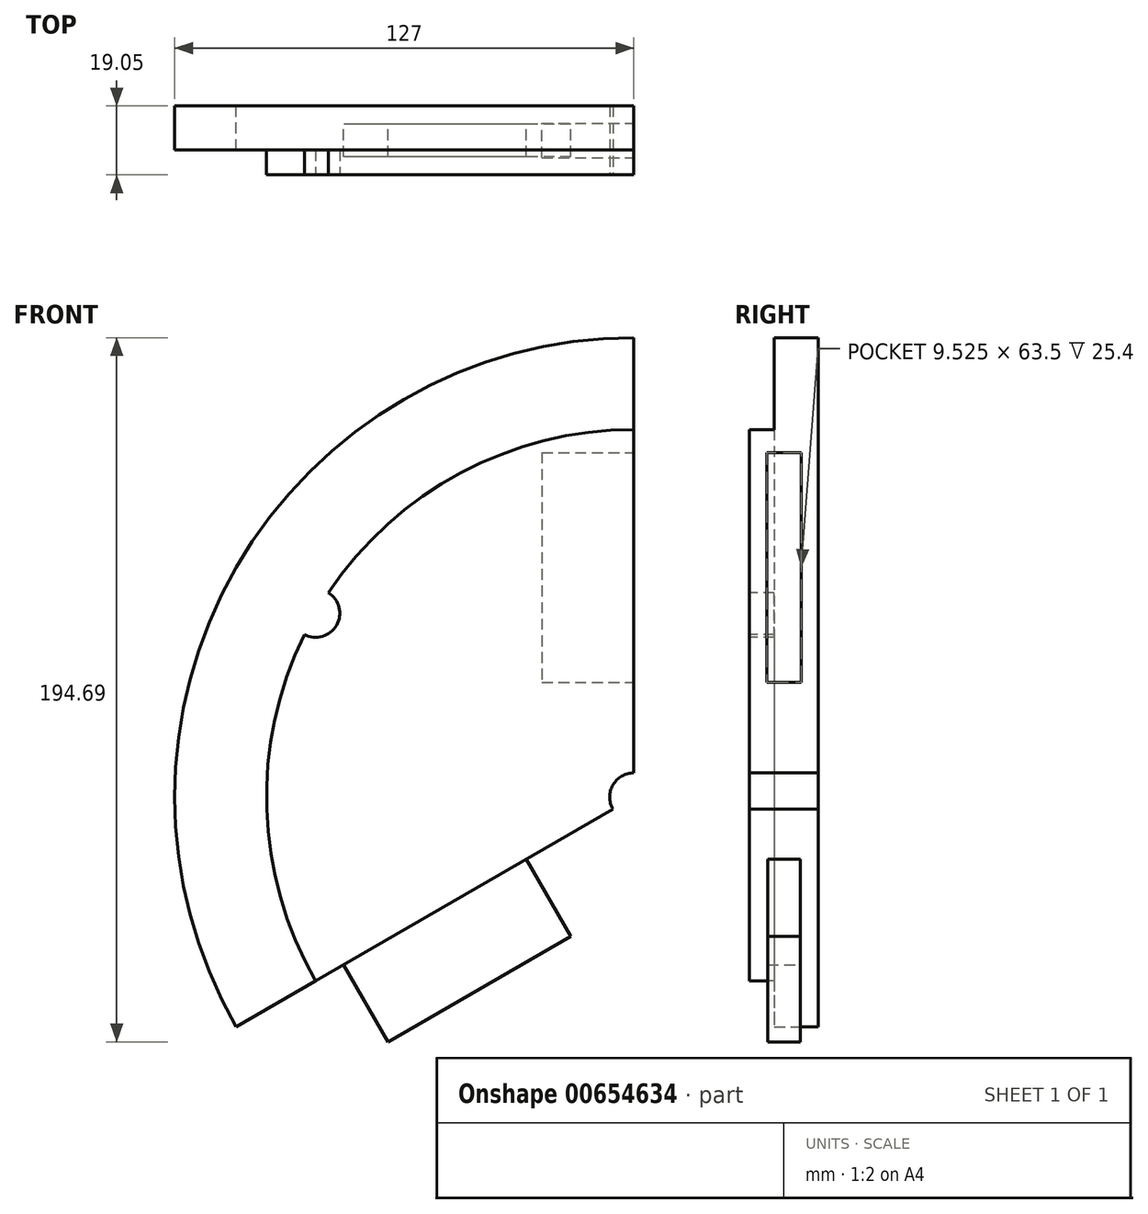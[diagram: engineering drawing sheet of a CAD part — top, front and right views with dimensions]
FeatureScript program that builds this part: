
annotation { "Feature Type Name" : "Feature", "Feature Type Description" : "" }
export const myFeature = defineFeature(function(context is Context, id is Id, definition is map)
    precondition{}
    {
        {
            var Q0;
            Q0=qCreatedBy(makeId("Front.planeOp"),FACE);
            var sketch = newSketch(context, id + "F0", { "sketchPlane" : qUnion([Q0])});
            skArc(sketch, "E0", {"start": v(0, 127) * mm, "mid": v(-109.99, 63.5) * mm, "end": v(-109.99, -63.5) * mm});
            skLineSegment(sketch, "E1", {"start": v(0, 0) * mm, "end": v(0, 127) * mm});
            skLineSegment(sketch, "E2", {"start": v(0, 0) * mm, "end": v(-109.99, -63.5) * mm});
            skArc(sketch, "E3", {"start": v(0, 101.6) * mm, "mid": v(-87.99, 50.8) * mm, "end": v(-87.99, -50.8) * mm});
            skLineSegment(sketch, "E4", {"start": v(0, 0) * mm, "end": v(-109.99, 63.5) * mm});
            skLineSegment(sketch, "E5", {"start": v(0, 0) * mm, "end": v(-63.5, 109.99) * mm});
            skLineSegment(sketch, "E6", {"start": v(0, 0) * mm, "end": v(-127, 0) * mm});
            skCircle(sketch, "E7", {"center": v(-50.8, 87.99) * mm, "radius": 6.6 * mm});
            skCircle(sketch, "E8", {"center": v(-101.6, 0) * mm, "radius": 6.6 * mm});
            skCircle(sketch, "E9", {"center": v(-87.99, 50.8) * mm, "radius": 6.6 * mm});
            skSolve(sketch);
        }
        {
            var Q0;
            {var subQ1=sQuery(id+"F0.wireOp",EDGE,"E0");var subQ6=sQuery(id+"F0.wireOp",EDGE,"E1");var subQ9=makeQuery(id+"F0.imprint","INTERSECT",VERTEX,{"derivedFrom":[subQ1,subQ6]});Q0=makeQuery(id+"F0.imprint","IMPRINT",FACE,{"disambiguationData":[TD([[makeQuery(id+"F0.imprint","IMPRINT",EDGE,{"disambiguationData":[TD([[subQ9,-1.0]])],"derivedFrom":subQ1}),1.0]])]});}
            var Q1;
            {var subQ1=sQuery(id+"F0.wireOp",EDGE,"E0");var subQ6=sQuery(id+"F0.wireOp",EDGE,"E2");var subQ9=makeQuery(id+"F0.imprint","INTERSECT",VERTEX,{"derivedFrom":[subQ1,subQ6]});Q1=makeQuery(id+"F0.imprint","IMPRINT",FACE,{"disambiguationData":[TD([[makeQuery(id+"F0.imprint","IMPRINT",EDGE,{"disambiguationData":[TD([[subQ9,1.0]])],"derivedFrom":subQ1}),1.0]])]});}
            var Q2;
            {var subQ1=sQuery(id+"F0.wireOp",EDGE,"E1");var subQ3=sQuery(id+"F0.wireOp",EDGE,"E3");var subQ4=makeQuery(id+"F0.imprint","INTERSECT",VERTEX,{"derivedFrom":[subQ1,subQ3]});Q2=makeQuery(id+"F0.imprint","IMPRINT",FACE,{"disambiguationData":[TD([[makeQuery(id+"F0.imprint","IMPRINT",EDGE,{"disambiguationData":[TD([[subQ4,-1.0]])],"derivedFrom":subQ3}),1.0]])]});}
            var Q3;
            {var subQ1=sQuery(id+"F0.wireOp",EDGE,"E2");var subQ3=sQuery(id+"F0.wireOp",EDGE,"E3");var subQ4=makeQuery(id+"F0.imprint","INTERSECT",VERTEX,{"derivedFrom":[subQ1,subQ3]});Q3=makeQuery(id+"F0.imprint","IMPRINT",FACE,{"disambiguationData":[TD([[makeQuery(id+"F0.imprint","IMPRINT",EDGE,{"disambiguationData":[TD([[subQ4,1.0]])],"derivedFrom":subQ3}),1.0]])]});}
            var Q4;
            {var subQ0=sQuery(id+"F0.wireOp",EDGE,"E4");var subQ1=sQuery(id+"F0.wireOp",EDGE,"E0");var subQ2=makeQuery(id+"F0.imprint","INTERSECT",VERTEX,{"derivedFrom":[subQ1,subQ0]});Q4=makeQuery(id+"F0.imprint","IMPRINT",FACE,{"disambiguationData":[TD([[makeQuery(id+"F0.imprint","IMPRINT",EDGE,{"disambiguationData":[TD([[subQ2,1.0]])],"derivedFrom":subQ1}),1.0]])]});}
            var Q5;
            {var subQ1=sQuery(id+"F0.wireOp",EDGE,"E0");var subQ9=sQuery(id+"F0.wireOp",EDGE,"E4");var subQ10=makeQuery(id+"F0.imprint","INTERSECT",VERTEX,{"derivedFrom":[subQ1,subQ9]});Q5=makeQuery(id+"F0.imprint","IMPRINT",FACE,{"disambiguationData":[TD([[makeQuery(id+"F0.imprint","IMPRINT",EDGE,{"disambiguationData":[TD([[subQ10,-1.0]])],"derivedFrom":subQ1}),1.0]])]});}
            var Q6;
            {var subQ0=sQuery(id+"F0.wireOp",EDGE,"E7");var subQ1=sQuery(id+"F0.wireOp",EDGE,"E3");var subQ2=makeQuery(id+"F0.imprint","INTERSECT",VERTEX,{"disambiguationData":[OD(1.0)],"derivedFrom":[subQ1,subQ0]});Q6=makeQuery(id+"F0.imprint","IMPRINT",FACE,{"disambiguationData":[TD([[makeQuery(id+"F0.imprint","IMPRINT",EDGE,{"disambiguationData":[TD([[subQ2,-1.0]])],"derivedFrom":subQ1}),1.0]])]});}
            var Q7;
            {var subQ1=sQuery(id+"F0.wireOp",EDGE,"E3");var subQ7=sQuery(id+"F0.wireOp",EDGE,"E9");var subQ9=makeQuery(id+"F0.imprint","INTERSECT",VERTEX,{"disambiguationData":[OD(1.0)],"derivedFrom":[subQ1,subQ7]});Q7=makeQuery(id+"F0.imprint","IMPRINT",FACE,{"disambiguationData":[TD([[makeQuery(id+"F0.imprint","IMPRINT",EDGE,{"disambiguationData":[TD([[subQ9,-1.0]])],"derivedFrom":subQ1}),1.0]])]});}
            var Q8;
            {var subQ0=sQuery(id+"F0.wireOp",EDGE,"E6");var subQ1=sQuery(id+"F0.wireOp",EDGE,"E3");var subQ2=makeQuery(id+"F0.imprint","INTERSECT",VERTEX,{"derivedFrom":[subQ1,subQ0]});Q8=makeQuery(id+"F0.imprint","IMPRINT",FACE,{"disambiguationData":[TD([[makeQuery(id+"F0.imprint","IMPRINT",EDGE,{"disambiguationData":[TD([[subQ2,-1.0]])],"derivedFrom":subQ1}),-1.0]])]});}
            var Q9;
            {var subQ0=sQuery(id+"F0.wireOp",EDGE,"E6");var subQ1=sQuery(id+"F0.wireOp",EDGE,"E3");var subQ2=makeQuery(id+"F0.imprint","INTERSECT",VERTEX,{"derivedFrom":[subQ1,subQ0]});Q9=makeQuery(id+"F0.imprint","IMPRINT",FACE,{"disambiguationData":[TD([[makeQuery(id+"F0.imprint","IMPRINT",EDGE,{"disambiguationData":[TD([[subQ2,-1.0]])],"derivedFrom":subQ1}),1.0]])]});}
            var Q10;
            {var subQ0=sQuery(id+"F0.wireOp",EDGE,"E8");var subQ1=sQuery(id+"F0.wireOp",EDGE,"E3");var subQ2=makeQuery(id+"F0.imprint","INTERSECT",VERTEX,{"disambiguationData":[OD(0.0)],"derivedFrom":[subQ1,subQ0]});Q10=makeQuery(id+"F0.imprint","IMPRINT",FACE,{"disambiguationData":[TD([[makeQuery(id+"F0.imprint","IMPRINT",EDGE,{"disambiguationData":[TD([[subQ2,-1.0]])],"derivedFrom":subQ1}),-1.0]])]});}
            var Q11;
            {var subQ0=sQuery(id+"F0.wireOp",EDGE,"E8");var subQ1=sQuery(id+"F0.wireOp",EDGE,"E3");var subQ2=makeQuery(id+"F0.imprint","INTERSECT",VERTEX,{"disambiguationData":[OD(0.0)],"derivedFrom":[subQ1,subQ0]});Q11=makeQuery(id+"F0.imprint","IMPRINT",FACE,{"disambiguationData":[TD([[makeQuery(id+"F0.imprint","IMPRINT",EDGE,{"disambiguationData":[TD([[subQ2,-1.0]])],"derivedFrom":subQ1}),1.0]])]});}
            var Q12;
            {var subQ0=sQuery(id+"F0.wireOp",EDGE,"E4");var subQ1=sQuery(id+"F0.wireOp",EDGE,"E3");var subQ2=makeQuery(id+"F0.imprint","INTERSECT",VERTEX,{"derivedFrom":[subQ1,subQ0]});Q12=makeQuery(id+"F0.imprint","IMPRINT",FACE,{"disambiguationData":[TD([[makeQuery(id+"F0.imprint","IMPRINT",EDGE,{"disambiguationData":[TD([[subQ2,-1.0]])],"derivedFrom":subQ1}),1.0]])]});}
            var Q13;
            {var subQ0=sQuery(id+"F0.wireOp",EDGE,"E4");var subQ1=sQuery(id+"F0.wireOp",EDGE,"E3");var subQ2=makeQuery(id+"F0.imprint","INTERSECT",VERTEX,{"derivedFrom":[subQ1,subQ0]});Q13=makeQuery(id+"F0.imprint","IMPRINT",FACE,{"disambiguationData":[TD([[makeQuery(id+"F0.imprint","IMPRINT",EDGE,{"disambiguationData":[TD([[subQ2,-1.0]])],"derivedFrom":subQ1}),-1.0]])]});}
            var Q14;
            {var subQ0=sQuery(id+"F0.wireOp",EDGE,"E9");var subQ1=sQuery(id+"F0.wireOp",EDGE,"E3");var subQ2=makeQuery(id+"F0.imprint","INTERSECT",VERTEX,{"disambiguationData":[OD(0.0)],"derivedFrom":[subQ1,subQ0]});Q14=makeQuery(id+"F0.imprint","IMPRINT",FACE,{"disambiguationData":[TD([[makeQuery(id+"F0.imprint","IMPRINT",EDGE,{"disambiguationData":[TD([[subQ2,-1.0]])],"derivedFrom":subQ1}),-1.0]])]});}
            var Q15;
            {var subQ0=sQuery(id+"F0.wireOp",EDGE,"E9");var subQ1=sQuery(id+"F0.wireOp",EDGE,"E3");var subQ2=makeQuery(id+"F0.imprint","INTERSECT",VERTEX,{"disambiguationData":[OD(0.0)],"derivedFrom":[subQ1,subQ0]});Q15=makeQuery(id+"F0.imprint","IMPRINT",FACE,{"disambiguationData":[TD([[makeQuery(id+"F0.imprint","IMPRINT",EDGE,{"disambiguationData":[TD([[subQ2,-1.0]])],"derivedFrom":subQ1}),1.0]])]});}
            var Q16;
            {var subQ0=sQuery(id+"F0.wireOp",EDGE,"E5");var subQ1=sQuery(id+"F0.wireOp",EDGE,"E3");var subQ2=makeQuery(id+"F0.imprint","INTERSECT",VERTEX,{"derivedFrom":[subQ1,subQ0]});Q16=makeQuery(id+"F0.imprint","IMPRINT",FACE,{"disambiguationData":[TD([[makeQuery(id+"F0.imprint","IMPRINT",EDGE,{"disambiguationData":[TD([[subQ2,-1.0]])],"derivedFrom":subQ1}),1.0]])]});}
            var Q17;
            {var subQ0=sQuery(id+"F0.wireOp",EDGE,"E7");var subQ1=sQuery(id+"F0.wireOp",EDGE,"E3");var subQ2=makeQuery(id+"F0.imprint","INTERSECT",VERTEX,{"disambiguationData":[OD(0.0)],"derivedFrom":[subQ1,subQ0]});Q17=makeQuery(id+"F0.imprint","IMPRINT",FACE,{"disambiguationData":[TD([[makeQuery(id+"F0.imprint","IMPRINT",EDGE,{"disambiguationData":[TD([[subQ2,-1.0]])],"derivedFrom":subQ1}),1.0]])]});}
            var Q18;
            {var subQ0=sQuery(id+"F0.wireOp",EDGE,"E7");var subQ1=sQuery(id+"F0.wireOp",EDGE,"E3");var subQ2=makeQuery(id+"F0.imprint","INTERSECT",VERTEX,{"disambiguationData":[OD(0.0)],"derivedFrom":[subQ1,subQ0]});Q18=makeQuery(id+"F0.imprint","IMPRINT",FACE,{"disambiguationData":[TD([[makeQuery(id+"F0.imprint","IMPRINT",EDGE,{"disambiguationData":[TD([[subQ2,-1.0]])],"derivedFrom":subQ1}),-1.0]])]});}
            var Q19;
            {var subQ0=sQuery(id+"F0.wireOp",EDGE,"E5");var subQ1=sQuery(id+"F0.wireOp",EDGE,"E3");var subQ2=makeQuery(id+"F0.imprint","INTERSECT",VERTEX,{"derivedFrom":[subQ1,subQ0]});Q19=makeQuery(id+"F0.imprint","IMPRINT",FACE,{"disambiguationData":[TD([[makeQuery(id+"F0.imprint","IMPRINT",EDGE,{"disambiguationData":[TD([[subQ2,-1.0]])],"derivedFrom":subQ1}),-1.0]])]});}
            extrude(context, id + "F1", {"entities" : qUnion([Q0, Q1, Q2, Q3, Q4, Q5, Q6, Q7, Q8, Q9, Q10, Q11, Q12, Q13, Q14, Q15, Q16, Q17, Q18, Q19]), "depth" : 19.05 * mm, "offsetDistance" : 25.4 * mm});
        }
        {
            var Q0;
            Q0=makeQuery(id+"F1.opExtrude","SWEPT_FACE",FACE,{"disambiguationData":[OSD([sQuery(id+"F0.wireOp",EDGE,"E1")])]});
            var sketch = newSketch(context, id + "F2", { "sketchPlane" : qUnion([Q0])});
            skLineSegment(sketch, "E10.bottom", {"start": v(0, 0) * mm, "end": v(-19.05, 0) * mm});
            skLineSegment(sketch, "E10.top", {"start": v(0, 127) * mm, "end": v(-19.05, 127) * mm});
            skLineSegment(sketch, "E10.left", {"start": v(0, 0) * mm, "end": v(0, 127) * mm});
            skLineSegment(sketch, "E10.right", {"start": v(-19.05, 0) * mm, "end": v(-19.05, 127) * mm});
            skLineSegment(sketch, "E11", {"start": v(-9.53, 0) * mm, "end": v(-9.53, 127) * mm});
            skLineSegment(sketch, "E12", {"start": v(-19.05, 63.5) * mm, "end": v(0, 63.5) * mm});
            skPoint(sketch, "E13", {"position": v(-9.53, 63.5) * mm});
            skLineSegment(sketch, "E14.bottom", {"start": v(-14.29, 95.25) * mm, "end": v(-4.76, 95.25) * mm});
            skLineSegment(sketch, "E14.top", {"start": v(-14.29, 31.75) * mm, "end": v(-4.76, 31.75) * mm});
            skLineSegment(sketch, "E14.left", {"start": v(-14.29, 95.25) * mm, "end": v(-14.29, 31.75) * mm});
            skLineSegment(sketch, "E14.right", {"start": v(-4.76, 95.25) * mm, "end": v(-4.76, 31.75) * mm});
            skSolve(sketch);
        }
        {
            var Q0;
            {var subQ0=sQuery(id+"F2.wireOp",EDGE,"E14.top");var subQ1=sQuery(id+"F2.wireOp",EDGE,"E11");var subQ2=makeQuery(id+"F2.imprint","INTERSECT",VERTEX,{"derivedFrom":[subQ1,subQ0]});Q0=makeQuery(id+"F2.imprint","IMPRINT",FACE,{"disambiguationData":[TD([[makeQuery(id+"F2.imprint","IMPRINT",EDGE,{"disambiguationData":[TD([[subQ2,-1.0]])],"derivedFrom":subQ1}),-1.0]])]});}
            var Q1;
            {var subQ0=sQuery(id+"F2.wireOp",EDGE,"E14.top");var subQ1=sQuery(id+"F2.wireOp",EDGE,"E11");var subQ2=makeQuery(id+"F2.imprint","INTERSECT",VERTEX,{"derivedFrom":[subQ1,subQ0]});Q1=makeQuery(id+"F2.imprint","IMPRINT",FACE,{"disambiguationData":[TD([[makeQuery(id+"F2.imprint","IMPRINT",EDGE,{"disambiguationData":[TD([[subQ2,-1.0]])],"derivedFrom":subQ1}),1.0]])]});}
            var Q2;
            {var subQ0=sQuery(id+"F2.wireOp",EDGE,"E12");var subQ1=sQuery(id+"F2.wireOp",EDGE,"E11");var subQ2=makeQuery(id+"F2.imprint","INTERSECT",VERTEX,{"derivedFrom":[subQ1,subQ0]});Q2=makeQuery(id+"F2.imprint","IMPRINT",FACE,{"disambiguationData":[TD([[makeQuery(id+"F2.imprint","IMPRINT",EDGE,{"disambiguationData":[TD([[subQ2,-1.0]])],"derivedFrom":subQ1}),1.0]])]});}
            var Q3;
            {var subQ0=sQuery(id+"F2.wireOp",EDGE,"E12");var subQ1=sQuery(id+"F2.wireOp",EDGE,"E11");var subQ2=makeQuery(id+"F2.imprint","INTERSECT",VERTEX,{"derivedFrom":[subQ1,subQ0]});Q3=makeQuery(id+"F2.imprint","IMPRINT",FACE,{"disambiguationData":[TD([[makeQuery(id+"F2.imprint","IMPRINT",EDGE,{"disambiguationData":[TD([[subQ2,-1.0]])],"derivedFrom":subQ1}),-1.0]])]});}
            extrude(context, id + "F3", {"entities" : qUnion([Q0, Q1, Q2, Q3]), "operationType" : NewBodyOperationType.REMOVE, "oppositeDirection" : true, "depth" : 25.4 * mm, "offsetDistance" : 25.4 * mm});
        }
        {
            var Q0;
            Q0=makeQuery(id+"F1.opExtrude","SWEPT_FACE",FACE,{"disambiguationData":[OSD([sQuery(id+"F0.wireOp",EDGE,"E2")])]});
            var sketch = newSketch(context, id + "F4", { "sketchPlane" : qUnion([Q0])});
            skLineSegment(sketch, "E15", {"start": v(-63.5, 0) * mm, "end": v(-63.5, 19.05) * mm});
            skLineSegment(sketch, "E16.bottom", {"start": v(-34.29, 14.03) * mm, "end": v(-92.7, 14.03) * mm});
            skLineSegment(sketch, "E16.top", {"start": v(-34.29, 5.02) * mm, "end": v(-92.7, 5.02) * mm});
            skLineSegment(sketch, "E16.left", {"start": v(-34.29, 14.03) * mm, "end": v(-34.29, 5.02) * mm});
            skLineSegment(sketch, "E16.right", {"start": v(-92.7, 14.03) * mm, "end": v(-92.7, 5.02) * mm});
            skPoint(sketch, "E16.middle", {"position": v(-63.5, 9.53) * mm});
            skSolve(sketch);
        }
        {
            var Q0;
            Q0 = qSketchRegion(id + "F4", true);
            extrude(context, id + "F5", {"entities" : qUnion([Q0]), "operationType" : NewBodyOperationType.ADD, "depth" : 24.64 * mm, "offsetDistance" : 25.4 * mm});
        }
        {
            var Q0;
            Q0=makeQuery(id+"F1.opExtrude","CAP_FACE",FACE,{"disambiguationData":[OSD([sQuery(id+"F0.wireOp",EDGE,"E0"),sQuery(id+"F0.wireOp",EDGE,"E1"),sQuery(id+"F0.wireOp",EDGE,"E2")])],"isStart":false});
            var sketch = newSketch(context, id + "F6", { "sketchPlane" : qUnion([Q0])});
            skLineSegment(sketch, "E17", {"start": v(0, 0) * mm, "end": v(-109.99, 63.5) * mm});
            skLineSegment(sketch, "E18", {"start": v(0, 0) * mm, "end": v(-63.5, 109.99) * mm});
            skLineSegment(sketch, "E19", {"start": v(0, 0) * mm, "end": v(-127, 0) * mm});
            skCircle(sketch, "E20", {"center": v(0, 0) * mm, "radius": 10.16 * mm});
            skCircle(sketch, "E21", {"center": v(0, 0) * mm, "radius": 101.6 * mm});
            skCircle(sketch, "E22", {"center": v(-50.8, 87.99) * mm, "radius": 6.66 * mm});
            skCircle(sketch, "E23", {"center": v(-87.99, 50.8) * mm, "radius": 6.67 * mm});
            skCircle(sketch, "E24", {"center": v(-101.6, 0) * mm, "radius": 6.67 * mm});
            skSolve(sketch);
        }
        {
            var Q0;
            {var subQ0=sQuery(id+"F6.wireOp",EDGE,"E24");var subQ1=sQuery(id+"F6.wireOp",EDGE,"E19");var subQ2=makeQuery(id+"F6.imprint","INTERSECT",VERTEX,{"disambiguationData":[OD(0.0)],"derivedFrom":[subQ1,subQ0]});Q0=makeQuery(id+"F6.imprint","IMPRINT",FACE,{"disambiguationData":[TD([[makeQuery(id+"F6.imprint","IMPRINT",EDGE,{"disambiguationData":[TD([[subQ2,-1.0]])],"derivedFrom":subQ1}),1.0]])]});}
            var Q1;
            {var subQ0=sQuery(id+"F6.wireOp",EDGE,"E21");var subQ1=sQuery(id+"F6.wireOp",EDGE,"E19");var subQ2=makeQuery(id+"F6.imprint","INTERSECT",VERTEX,{"derivedFrom":[subQ1,subQ0]});Q1=makeQuery(id+"F6.imprint","IMPRINT",FACE,{"disambiguationData":[TD([[makeQuery(id+"F6.imprint","IMPRINT",EDGE,{"disambiguationData":[TD([[subQ2,-1.0]])],"derivedFrom":subQ1}),1.0]])]});}
            var Q2;
            {var subQ0=sQuery(id+"F6.wireOp",EDGE,"E21");var subQ1=sQuery(id+"F6.wireOp",EDGE,"E19");var subQ2=makeQuery(id+"F6.imprint","INTERSECT",VERTEX,{"derivedFrom":[subQ1,subQ0]});Q2=makeQuery(id+"F6.imprint","IMPRINT",FACE,{"disambiguationData":[TD([[makeQuery(id+"F6.imprint","IMPRINT",EDGE,{"disambiguationData":[TD([[subQ2,-1.0]])],"derivedFrom":subQ1}),-1.0]])]});}
            var Q3;
            {var subQ0=sQuery(id+"F6.wireOp",EDGE,"E24");var subQ1=sQuery(id+"F6.wireOp",EDGE,"E19");var subQ2=makeQuery(id+"F6.imprint","INTERSECT",VERTEX,{"disambiguationData":[OD(0.0)],"derivedFrom":[subQ1,subQ0]});Q3=makeQuery(id+"F6.imprint","IMPRINT",FACE,{"disambiguationData":[TD([[makeQuery(id+"F6.imprint","IMPRINT",EDGE,{"disambiguationData":[TD([[subQ2,-1.0]])],"derivedFrom":subQ1}),-1.0]])]});}
            var Q4;
            {var subQ0=sQuery(id+"F6.wireOp",EDGE,"E23");var subQ1=sQuery(id+"F6.wireOp",EDGE,"E17");var subQ2=makeQuery(id+"F6.imprint","INTERSECT",VERTEX,{"disambiguationData":[OD(0.0)],"derivedFrom":[subQ1,subQ0]});Q4=makeQuery(id+"F6.imprint","IMPRINT",FACE,{"disambiguationData":[TD([[makeQuery(id+"F6.imprint","IMPRINT",EDGE,{"disambiguationData":[TD([[subQ2,-1.0]])],"derivedFrom":subQ1}),1.0]])]});}
            var Q5;
            {var subQ0=sQuery(id+"F6.wireOp",EDGE,"E21");var subQ1=sQuery(id+"F6.wireOp",EDGE,"E17");var subQ2=makeQuery(id+"F6.imprint","INTERSECT",VERTEX,{"derivedFrom":[subQ1,subQ0]});Q5=makeQuery(id+"F6.imprint","IMPRINT",FACE,{"disambiguationData":[TD([[makeQuery(id+"F6.imprint","IMPRINT",EDGE,{"disambiguationData":[TD([[subQ2,-1.0]])],"derivedFrom":subQ1}),1.0]])]});}
            var Q6;
            {var subQ0=sQuery(id+"F6.wireOp",EDGE,"E21");var subQ1=sQuery(id+"F6.wireOp",EDGE,"E17");var subQ2=makeQuery(id+"F6.imprint","INTERSECT",VERTEX,{"derivedFrom":[subQ1,subQ0]});Q6=makeQuery(id+"F6.imprint","IMPRINT",FACE,{"disambiguationData":[TD([[makeQuery(id+"F6.imprint","IMPRINT",EDGE,{"disambiguationData":[TD([[subQ2,-1.0]])],"derivedFrom":subQ1}),-1.0]])]});}
            var Q7;
            {var subQ0=sQuery(id+"F6.wireOp",EDGE,"E23");var subQ1=sQuery(id+"F6.wireOp",EDGE,"E17");var subQ2=makeQuery(id+"F6.imprint","INTERSECT",VERTEX,{"disambiguationData":[OD(0.0)],"derivedFrom":[subQ1,subQ0]});Q7=makeQuery(id+"F6.imprint","IMPRINT",FACE,{"disambiguationData":[TD([[makeQuery(id+"F6.imprint","IMPRINT",EDGE,{"disambiguationData":[TD([[subQ2,-1.0]])],"derivedFrom":subQ1}),-1.0]])]});}
            var Q8;
            {var subQ0=sQuery(id+"F6.wireOp",EDGE,"E22");var subQ1=sQuery(id+"F6.wireOp",EDGE,"E18");var subQ2=makeQuery(id+"F6.imprint","INTERSECT",VERTEX,{"disambiguationData":[OD(0.0)],"derivedFrom":[subQ1,subQ0]});Q8=makeQuery(id+"F6.imprint","IMPRINT",FACE,{"disambiguationData":[TD([[makeQuery(id+"F6.imprint","IMPRINT",EDGE,{"disambiguationData":[TD([[subQ2,-1.0]])],"derivedFrom":subQ1}),1.0]])]});}
            var Q9;
            {var subQ0=sQuery(id+"F6.wireOp",EDGE,"E21");var subQ1=sQuery(id+"F6.wireOp",EDGE,"E18");var subQ2=makeQuery(id+"F6.imprint","INTERSECT",VERTEX,{"derivedFrom":[subQ1,subQ0]});Q9=makeQuery(id+"F6.imprint","IMPRINT",FACE,{"disambiguationData":[TD([[makeQuery(id+"F6.imprint","IMPRINT",EDGE,{"disambiguationData":[TD([[subQ2,-1.0]])],"derivedFrom":subQ1}),-1.0]])]});}
            var Q10;
            {var subQ0=sQuery(id+"F6.wireOp",EDGE,"E21");var subQ1=sQuery(id+"F6.wireOp",EDGE,"E18");var subQ2=makeQuery(id+"F6.imprint","INTERSECT",VERTEX,{"derivedFrom":[subQ1,subQ0]});Q10=makeQuery(id+"F6.imprint","IMPRINT",FACE,{"disambiguationData":[TD([[makeQuery(id+"F6.imprint","IMPRINT",EDGE,{"disambiguationData":[TD([[subQ2,-1.0]])],"derivedFrom":subQ1}),1.0]])]});}
            var Q11;
            {var subQ0=sQuery(id+"F6.wireOp",EDGE,"E22");var subQ1=sQuery(id+"F6.wireOp",EDGE,"E18");var subQ2=makeQuery(id+"F6.imprint","INTERSECT",VERTEX,{"disambiguationData":[OD(0.0)],"derivedFrom":[subQ1,subQ0]});Q11=makeQuery(id+"F6.imprint","IMPRINT",FACE,{"disambiguationData":[TD([[makeQuery(id+"F6.imprint","IMPRINT",EDGE,{"disambiguationData":[TD([[subQ2,-1.0]])],"derivedFrom":subQ1}),-1.0]])]});}
            extrude(context, id + "F7", {"entities" : qUnion([Q0, Q1, Q2, Q3, Q4, Q5, Q6, Q7, Q8, Q9, Q10, Q11]), "operationType" : NewBodyOperationType.REMOVE, "oppositeDirection" : true, "depth" : 6.86 * mm, "offsetDistance" : 25.4 * mm});
        }
        {
            var Q0;
            Q0=makeQuery(id+"F1.opExtrude","CAP_FACE",FACE,{"disambiguationData":[OSD([sQuery(id+"F0.wireOp",EDGE,"E0"),sQuery(id+"F0.wireOp",EDGE,"E1"),sQuery(id+"F0.wireOp",EDGE,"E2")])],"isStart":false});
            var sketch = newSketch(context, id + "F8", { "sketchPlane" : qUnion([Q0])});
            skCircle(sketch, "E25", {"center": v(0, 0) * mm, "radius": 6.67 * mm});
            skSolve(sketch);
        }
        {
            var Q0;
            Q0 = qSketchRegion(id + "F8", true);
            extrude(context, id + "F9", {"entities" : qUnion([Q0]), "operationType" : NewBodyOperationType.REMOVE, "oppositeDirection" : true, "depth" : 25.4 * mm, "offsetDistance" : 25.4 * mm});
        }
    });
